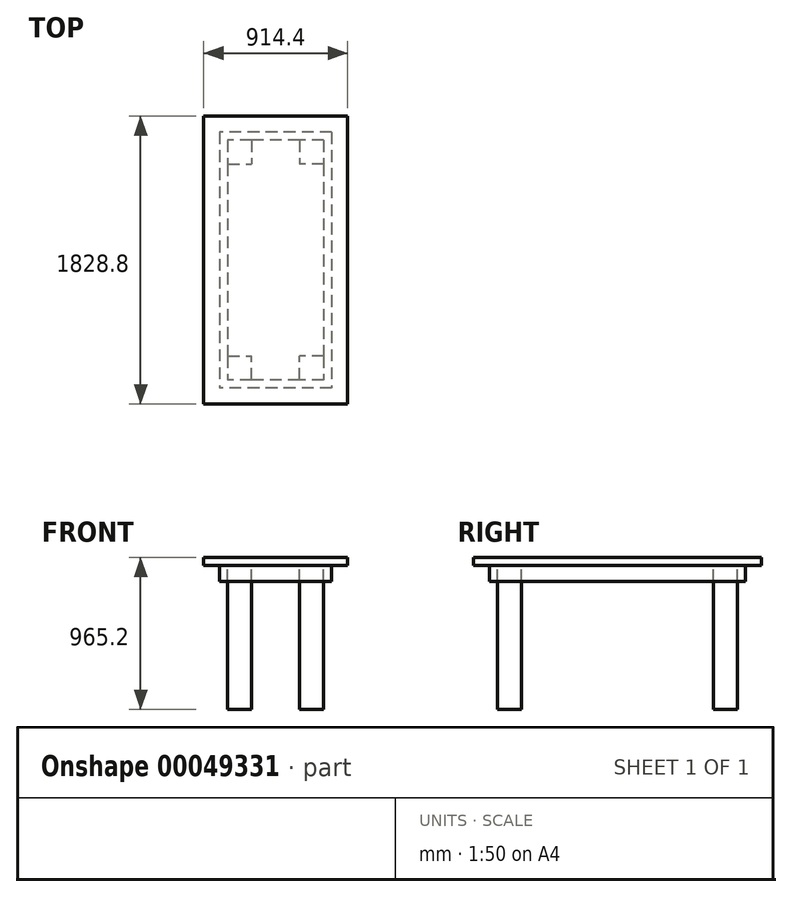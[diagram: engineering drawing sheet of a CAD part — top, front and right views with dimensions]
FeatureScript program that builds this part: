
annotation { "Feature Type Name" : "Feature", "Feature Type Description" : "" }
export const myFeature = defineFeature(function(context is Context, id is Id, definition is map)
    precondition{}
    {
        {
            var Q0;
            Q0=qCreatedBy(makeId("Top.planeOp"),FACE);
            var sketch = newSketch(context, id + "F0", { "sketchPlane" : qUnion([Q0])});
            skLineSegment(sketch, "E0.rect.bottom", {"start": v(457.2, 914.4) * mm, "end": v(-457.2, 914.4) * mm});
            skLineSegment(sketch, "E0.rect.top", {"start": v(457.2, -914.4) * mm, "end": v(-457.2, -914.4) * mm});
            skLineSegment(sketch, "E0.rect.left", {"start": v(457.2, 914.4) * mm, "end": v(457.2, -914.4) * mm});
            skLineSegment(sketch, "E0.rect.right", {"start": v(-457.2, 914.4) * mm, "end": v(-457.2, -914.4) * mm});
            skPoint(sketch, "E0.rect.middle", {"position": v(0, 0) * mm});
            skSolve(sketch);
        }
        {
            var Q0;
            Q0=makeQuery(id+"F0.imprint","IMPRINT",FACE,{"disambiguationData":[TD([[makeQuery(id+"F0.imprint","IMPRINT",EDGE,{"derivedFrom":sQuery(id+"F0.wireOp",EDGE,"E0.rect.bottom")}),1.0]])]});
            extrude(context, id + "F1", {"entities" : qUnion([Q0]), "oppositeDirection" : true, "depth" : 50.8 * mm});
        }
        {
            var Q0;
            Q0=makeQuery(id+"F1.opExtrude","CAP_FACE",FACE,{"disambiguationData":[OSD([sQuery(id+"F0.wireOp",EDGE,"E0.rect.bottom"),sQuery(id+"F0.wireOp",EDGE,"E0.rect.top"),sQuery(id+"F0.wireOp",EDGE,"E0.rect.left"),sQuery(id+"F0.wireOp",EDGE,"E0.rect.right")])],"isStart":false});
            var sketch = newSketch(context, id + "F2", { "sketchPlane" : qUnion([Q0])});
            skLineSegment(sketch, "E1.rect.bottom", {"start": v(304.8, -762) * mm, "end": v(-304.8, -762) * mm});
            skLineSegment(sketch, "E1.rect.top", {"start": v(304.8, 762) * mm, "end": v(-304.8, 762) * mm});
            skLineSegment(sketch, "E1.rect.left", {"start": v(304.8, -762) * mm, "end": v(304.8, 762) * mm});
            skLineSegment(sketch, "E1.rect.right", {"start": v(-304.8, -762) * mm, "end": v(-304.8, 762) * mm});
            skPoint(sketch, "E1.rect.middle", {"position": v(0, 0) * mm});
            skLineSegment(sketch, "E2.0", {"start": v(355.6, 812.8) * mm, "end": v(-355.6, 812.8) * mm});
            skLineSegment(sketch, "E2.1", {"start": v(355.6, -812.8) * mm, "end": v(355.6, 812.8) * mm});
            skLineSegment(sketch, "E2.2", {"start": v(355.6, -812.8) * mm, "end": v(-355.6, -812.8) * mm});
            skLineSegment(sketch, "E2.3", {"start": v(-355.6, -812.8) * mm, "end": v(-355.6, 812.8) * mm});
            skSolve(sketch);
        }
        {
            var Q0;
            Q0=makeQuery(id+"F2.imprint","IMPRINT",FACE,{"disambiguationData":[TD([[makeQuery(id+"F2.imprint","IMPRINT",EDGE,{"derivedFrom":sQuery(id+"F2.wireOp",EDGE,"E1.rect.bottom")}),1.0]])]});
            var Q1;
            Q1=sQuery(id+"F2.wireOp",EDGE,"E2.2");
            var Q2;
            Q2=sQuery(id+"F2.wireOp",EDGE,"E1.rect.bottom");
            var Q3;
            Q3=sQuery(id+"F2.wireOp",EDGE,"E1.rect.left");
            var Q4;
            Q4=sQuery(id+"F2.wireOp",EDGE,"E2.1");
            extrude(context, id + "F3", {"entities" : qUnion([Q0]), "operationType" : NewBodyOperationType.ADD, "surfaceEntities" : qUnion([Q1, Q2, Q3, Q4]), "depth" : 101.6 * mm});
        }
        {
            var Q0;
            Q0=makeQuery(id+"F3.boolean.opBoolean","SPLIT",FACE,{"disambiguationData":[TD([makeQuery(id+"F3.opExtrude","SWEPT_FACE",FACE,{"disambiguationData":[OSD([sQuery(id+"F2.wireOp",EDGE,"E1.rect.bottom")])]})])],"derivedFrom":makeQuery(id+"F1.opExtrude","CAP_FACE",FACE,{"disambiguationData":[OSD([sQuery(id+"F0.wireOp",EDGE,"E0.rect.bottom"),sQuery(id+"F0.wireOp",EDGE,"E0.rect.top"),sQuery(id+"F0.wireOp",EDGE,"E0.rect.left"),sQuery(id+"F0.wireOp",EDGE,"E0.rect.right")])],"isStart":false})});
            var sketch = newSketch(context, id + "F5", { "sketchPlane" : qUnion([Q0])});
            skLineSegment(sketch, "E3.bottom", {"start": v(-304.8, -762) * mm, "end": v(-152.4, -762) * mm});
            skLineSegment(sketch, "E3.top", {"start": v(-304.8, -609.6) * mm, "end": v(-152.4, -609.6) * mm});
            skLineSegment(sketch, "E3.left", {"start": v(-304.8, -762) * mm, "end": v(-304.8, -609.6) * mm});
            skLineSegment(sketch, "E3.right", {"start": v(-152.4, -762) * mm, "end": v(-152.4, -609.6) * mm});
            skLineSegment(sketch, "E4", {"start": v(-304.8, 0) * mm, "end": v(304.8, 0) * mm, "construction": true});
            skLineSegment(sketch, "E5", {"start": v(304.8, 0) * mm, "end": v(0, -762) * mm, "construction": true});
            skLineSegment(sketch, "E6", {"start": v(0, -762) * mm, "end": v(0, 762) * mm, "construction": true});
            skLineSegment(sketch, "E7.MirrorCS", {"start": v(-304.8, 609.6) * mm, "end": v(-152.4, 609.6) * mm});
            skLineSegment(sketch, "E8.MirrorCS", {"start": v(-152.4, 762) * mm, "end": v(-152.4, 609.6) * mm});
            skLineSegment(sketch, "E9.MirrorCS", {"start": v(-304.8, 762) * mm, "end": v(-152.4, 762) * mm});
            skLineSegment(sketch, "E10.MirrorCS", {"start": v(152.4, -762) * mm, "end": v(152.4, -609.6) * mm});
            skLineSegment(sketch, "E11.MirrorCS", {"start": v(304.8, -609.6) * mm, "end": v(152.4, -609.6) * mm});
            skLineSegment(sketch, "E12.MirrorCS", {"start": v(304.8, -762) * mm, "end": v(152.4, -762) * mm});
            skLineSegment(sketch, "E13.MirrorCS", {"start": v(304.8, -762) * mm, "end": v(304.8, -609.6) * mm});
            skLineSegment(sketch, "E14.MirrorCS", {"start": v(304.8, 609.6) * mm, "end": v(152.4, 609.6) * mm});
            skLineSegment(sketch, "E15.MirrorCS", {"start": v(152.4, 762) * mm, "end": v(152.4, 609.6) * mm});
            skLineSegment(sketch, "E16.MirrorCS", {"start": v(304.8, 762) * mm, "end": v(152.4, 762) * mm});
            skLineSegment(sketch, "E17.MirrorCS", {"start": v(-304.8, 762) * mm, "end": v(-304.8, 609.6) * mm});
            skLineSegment(sketch, "E18.MirrorCS", {"start": v(304.8, 762) * mm, "end": v(304.8, 609.6) * mm});
            skSolve(sketch);
        }
        {
            var Q0;
            Q0 = qSketchRegion(id + "F5", true);
            extrude(context, id + "F4", {"entities" : qUnion([Q0]), "operationType" : NewBodyOperationType.ADD, "depth" : 914.4 * mm});
        }
    });
